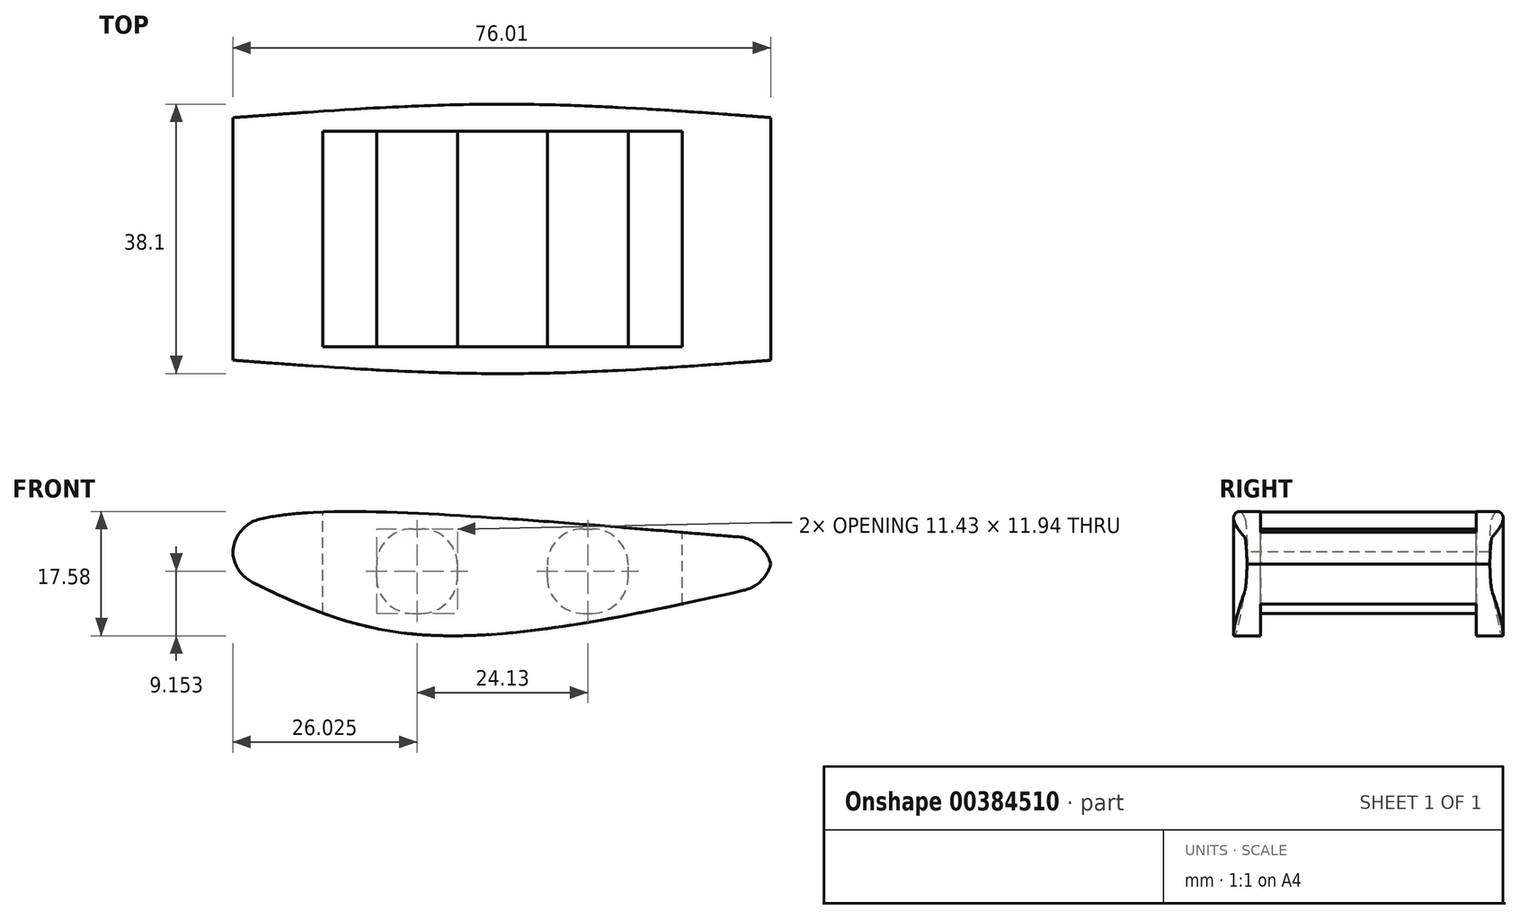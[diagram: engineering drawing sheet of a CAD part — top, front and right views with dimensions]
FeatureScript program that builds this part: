
annotation { "Feature Type Name" : "Feature", "Feature Type Description" : "" }
export const myFeature = defineFeature(function(context is Context, id is Id, definition is map)
    precondition{}
    {
        {
            var Q0;
            Q0=qCreatedBy(makeId("Top.planeOp"),FACE);
            var sketch = newSketch(context, id + "F0", { "sketchPlane" : qUnion([Q0])});
            skLineSegment(sketch, "E0.bottom", {"start": v(0, 0) * mm, "end": v(76.2, 0) * mm});
            skLineSegment(sketch, "E0.top", {"start": v(0, -38.1) * mm, "end": v(76.2, -38.1) * mm});
            skLineSegment(sketch, "E0.left", {"start": v(0, 0) * mm, "end": v(0, -38.1) * mm});
            skLineSegment(sketch, "E0.right", {"start": v(76.2, 0) * mm, "end": v(76.2, -38.1) * mm});
            skSolve(sketch);
        }
        {
            var Q0;
            Q0 = qSketchRegion(id + "F0", true);
            extrude(context, id + "F1", {"entities" : qUnion([Q0]), "depth" : 22.86 * mm});
        }
        {
            var Q0;
            Q0=makeQuery(id+"F1.opExtrude","SWEPT_FACE",FACE,{"disambiguationData":[OSD([sQuery(id+"F0.wireOp",EDGE,"E0.top")])]});
            cPlane(context, id + "F2", {"entities" : qUnion([Q0]), "cplaneType" : CPlaneType.OFFSET, "offset" : 0 * mm, "width" : 152.4 * mm, "height" : 152.4 * mm});
        }
        {
            var Q0;
            Q0=qCreatedBy(id+"F2.planeOp",FACE);
            var sketch = newSketch(context, id + "F3", { "sketchPlane" : qUnion([Q0])});
            skFitSpline(sketch, "E1", {"points": [v(0, 17.78) * mm, v(15.3, 19.73) * mm, v(76.18, 15.83) * mm, v(79.63, 15.83) * mm], "startDerivative": vector(36.87, 9.02) * mm, "endDerivative": vector(15.57, 0.79) * mm});
            skLineSegment(sketch, "E2", {"start": v(76.18, 15.83) * mm, "end": v(76.18, 9.48) * mm});
            skFitSpline(sketch, "E3", {"points": [v(76.18, 9.48) * mm, v(25.54, 2.4) * mm, v(0, 11.1) * mm], "startDerivative": vector(-95.9, -21.73) * mm, "endDerivative": vector(-55.13, 27.65) * mm});
            skLineSegment(sketch, "E4", {"start": v(0, 11.1) * mm, "end": v(0, 17.78) * mm});
            skSolve(sketch);
        }
        {
            var Q0;
            Q0=makeQuery(id+"F1.opExtrude","SWEPT_FACE",FACE,{"disambiguationData":[OSD([sQuery(id+"F0.wireOp",EDGE,"E0.top")])]});
            extrude(context, id + "F4", {"entities" : qUnion([Q0]), "operationType" : NewBodyOperationType.REMOVE, "oppositeDirection" : true, "depth" : 38.1 * mm});
        }
        {
            var Q0;
            {var subQ2=sQuery(id+"F3.wireOp",EDGE,"E2");Q0=makeQuery(id+"F3.imprint","IMPRINT",FACE,{"disambiguationData":[TD([[makeQuery(id+"F3.imprint","IMPRINT",EDGE,{"derivedFrom":subQ2}),-1.0]])]});}
            extrude(context, id + "F5", {"entities" : qUnion([Q0]), "oppositeDirection" : true, "depth" : 38.1 * mm});
        }
        {
            var Q0;
            Q0=qCreatedBy(makeId("Top.planeOp"),FACE);
            cPlane(context, id + "F6", {"entities" : qUnion([Q0]), "cplaneType" : CPlaneType.OFFSET, "offset" : 19.8 * mm, "width" : 152.4 * mm, "height" : 152.4 * mm});
        }
        {
            var Q0;
            Q0=qCreatedBy(id+"F6.planeOp",FACE);
            var sketch = newSketch(context, id + "F7", { "sketchPlane" : qUnion([Q0])});
            skLineSegment(sketch, "E5", {"start": v(0, 0) * mm, "end": v(0, -3.81) * mm});
            skLineSegment(sketch, "E6", {"start": v(0, -3.81) * mm, "end": v(76.2, -3.81) * mm});
            skLineSegment(sketch, "E7", {"start": v(0, 0) * mm, "end": v(38.1, 0) * mm});
            skLineSegment(sketch, "E8", {"start": v(76.2, -3.81) * mm, "end": v(76.2, -1.9) * mm});
            skLineSegment(sketch, "E9", {"start": v(0, -3.81) * mm, "end": v(0, -1.9) * mm});
            skFitSpline(sketch, "E10", {"points": [v(0, -1.9) * mm, v(38.1, 0) * mm, v(76.2, -1.9) * mm], "startDerivative": vector(76.2, 5.71) * mm, "endDerivative": vector(76.2, -5.71) * mm});
            skLineSegment(sketch, "E11", {"start": v(0, -3.81) * mm, "end": v(0, -34.29) * mm});
            skLineSegment(sketch, "E12", {"start": v(0, -34.29) * mm, "end": v(0, -36.2) * mm});
            skLineSegment(sketch, "E13", {"start": v(0, -34.29) * mm, "end": v(76.2, -34.29) * mm});
            skLineSegment(sketch, "E14", {"start": v(76.2, -34.29) * mm, "end": v(76.2, -36.2) * mm});
            skLineSegment(sketch, "E15", {"start": v(0, -34.29) * mm, "end": v(0, -38.1) * mm});
            skLineSegment(sketch, "E16", {"start": v(0, -38.1) * mm, "end": v(38.1, -38.1) * mm});
            skFitSpline(sketch, "E17", {"points": [v(0, -36.2) * mm, v(38.1, -38.1) * mm, v(76.2, -36.2) * mm], "startDerivative": vector(76.2, -5.71) * mm, "endDerivative": vector(76.2, 5.71) * mm});
            skLineSegment(sketch, "E18", {"start": v(38.1, 0) * mm, "end": v(76.2, 0) * mm});
            skLineSegment(sketch, "E19", {"start": v(76.2, 0) * mm, "end": v(76.2, -1.9) * mm});
            skLineSegment(sketch, "E20", {"start": v(38.1, -38.1) * mm, "end": v(76.2, -38.1) * mm});
            skLineSegment(sketch, "E21", {"start": v(76.2, -38.1) * mm, "end": v(76.2, -36.2) * mm});
            skSolve(sketch);
        }
        {
            var Q0;
            {var subQ0=sQuery(id+"F7.wireOp",EDGE,"E5");Q0=makeQuery(id+"F7.imprint","IMPRINT",FACE,{"disambiguationData":[TD([[makeQuery(id+"F7.imprint","IMPRINT",EDGE,{"derivedFrom":subQ0}),1.0]])]});}
            var Q1;
            {var subQ0=sQuery(id+"F7.wireOp",EDGE,"E16");Q1=makeQuery(id+"F7.imprint","IMPRINT",FACE,{"disambiguationData":[TD([[makeQuery(id+"F7.imprint","IMPRINT",EDGE,{"derivedFrom":subQ0}),1.0]])]});}
            var Q2;
            {var subQ2=sQuery(id+"F7.wireOp",EDGE,"E20");Q2=makeQuery(id+"F7.imprint","IMPRINT",FACE,{"disambiguationData":[TD([[makeQuery(id+"F7.imprint","IMPRINT",EDGE,{"derivedFrom":subQ2}),1.0]])]});}
            var Q3;
            {var subQ0=sQuery(id+"F7.wireOp",EDGE,"E18");Q3=makeQuery(id+"F7.imprint","IMPRINT",FACE,{"disambiguationData":[TD([[makeQuery(id+"F7.imprint","IMPRINT",EDGE,{"derivedFrom":subQ0}),-1.0]])]});}
            extrude(context, id + "F8", {"entities" : qUnion([Q0, Q1, Q2, Q3]), "operationType" : NewBodyOperationType.REMOVE, "oppositeDirection" : true, "depth" : 25.4 * mm});
        }
        {
            var Q0;
            Q0=qCreatedBy(id+"F6.planeOp",FACE);
            var sketch = newSketch(context, id + "F9", { "sketchPlane" : qUnion([Q0])});
            skLineSegment(sketch, "E22", {"start": v(0, 0) * mm, "end": v(0, -19.05) * mm});
            skLineSegment(sketch, "E23", {"start": v(0, -19.05) * mm, "end": v(12.7, -19.05) * mm});
            skLineSegment(sketch, "E24", {"start": v(12.7, -19.05) * mm, "end": v(12.7, -3.8) * mm});
            skLineSegment(sketch, "E25", {"start": v(12.7, -19.05) * mm, "end": v(12.7, -34.29) * mm});
            skLineSegment(sketch, "E26", {"start": v(63.5, -19.05) * mm, "end": v(63.5, -3.8) * mm});
            skLineSegment(sketch, "E27", {"start": v(63.5, -19.05) * mm, "end": v(63.5, -34.29) * mm});
            skLineSegment(sketch, "E28.trimOffspring", {"start": v(63.5, -19.05) * mm, "end": v(76.2, -19.05) * mm});
            skLineSegment(sketch, "E29", {"start": v(63.5, -19.05) * mm, "end": v(55.88, -19.05) * mm});
            skLineSegment(sketch, "E30", {"start": v(55.88, -19.05) * mm, "end": v(55.88, -3.8) * mm});
            skLineSegment(sketch, "E31", {"start": v(55.88, -19.05) * mm, "end": v(55.88, -34.3) * mm});
            skLineSegment(sketch, "E32", {"start": v(55.88, -34.3) * mm, "end": v(63.5, -34.3) * mm});
            skLineSegment(sketch, "E33", {"start": v(55.88, -3.8) * mm, "end": v(63.5, -3.8) * mm});
            skLineSegment(sketch, "E34", {"start": v(12.7, -19.05) * mm, "end": v(20.32, -19.05) * mm});
            skLineSegment(sketch, "E35", {"start": v(20.32, -19.05) * mm, "end": v(20.32, -3.8) * mm});
            skLineSegment(sketch, "E36", {"start": v(20.32, -19.05) * mm, "end": v(20.32, -34.29) * mm});
            skLineSegment(sketch, "E37", {"start": v(12.7, -34.29) * mm, "end": v(20.32, -34.29) * mm});
            skLineSegment(sketch, "E38", {"start": v(12.7, -3.8) * mm, "end": v(20.32, -3.8) * mm});
            skSolve(sketch);
        }
        {
            var Q0;
            Q0 = qSketchRegion(id + "F9", true);
            extrude(context, id + "F10", {"entities" : qUnion([Q0]), "operationType" : NewBodyOperationType.REMOVE, "oppositeDirection" : true, "depth" : 25.4 * mm});
        }
        {
            var Q0;
            Q0=qCreatedBy(id+"F6.planeOp",FACE);
            var sketch = newSketch(context, id + "F11", { "sketchPlane" : qUnion([Q0])});
            skLineSegment(sketch, "E39", {"start": v(0, 0) * mm, "end": v(0, -19.05) * mm});
            skLineSegment(sketch, "E40", {"start": v(31.75, -19.05) * mm, "end": v(31.75, -34.3) * mm});
            skLineSegment(sketch, "E41", {"start": v(31.75, -19.05) * mm, "end": v(31.75, -3.8) * mm});
            skLineSegment(sketch, "E42", {"start": v(44.45, -19.05) * mm, "end": v(44.45, -3.8) * mm});
            skLineSegment(sketch, "E43", {"start": v(44.45, -19.05) * mm, "end": v(44.45, -34.3) * mm});
            skLineSegment(sketch, "E44", {"start": v(31.75, -34.3) * mm, "end": v(44.45, -34.3) * mm});
            skLineSegment(sketch, "E45", {"start": v(31.75, -3.8) * mm, "end": v(44.45, -3.8) * mm});
            skSolve(sketch);
        }
        {
            var Q0;
            Q0 = qSketchRegion(id + "F11", true);
            extrude(context, id + "F12", {"entities" : qUnion([Q0]), "operationType" : NewBodyOperationType.REMOVE, "oppositeDirection" : true, "depth" : 25.4 * mm});
        }
        {
            var Q0;
            Q0=qCreatedBy(id+"F6.planeOp",FACE);
            var sketch = newSketch(context, id + "F13", { "sketchPlane" : qUnion([Q0])});
            skLineSegment(sketch, "E46", {"start": v(0, 0) * mm, "end": v(0, -19.05) * mm});
            skLineSegment(sketch, "E47", {"start": v(0, -19.05) * mm, "end": v(12.7, -19.05) * mm});
            skLineSegment(sketch, "E48", {"start": v(12.7, -19.05) * mm, "end": v(12.7, -34.3) * mm});
            skLineSegment(sketch, "E49.bottom", {"start": v(12.7, -34.3) * mm, "end": v(63.5, -34.3) * mm});
            skLineSegment(sketch, "E49.top", {"start": v(12.7, -3.8) * mm, "end": v(63.5, -3.8) * mm});
            skLineSegment(sketch, "E49.left", {"start": v(12.7, -34.3) * mm, "end": v(12.7, -3.8) * mm});
            skLineSegment(sketch, "E49.right", {"start": v(63.5, -34.29) * mm, "end": v(63.5, -3.8) * mm});
            skSolve(sketch);
        }
        {
            var Q0;
            Q0 = qSketchRegion(id + "F13", true);
            extrude(context, id + "F14", {"entities" : qUnion([Q0]), "operationType" : NewBodyOperationType.REMOVE, "depth" : -2.54 * mm});
        }
        {
            var Q0;
            Q0=makeQuery(id+"F14.boolean.opBoolean","INTERSECT",EDGE,{"derivedFrom":[makeQuery(id+"F10.boolean.opBoolean","COPY",FACE,{"derivedFrom":makeQuery(id+"F10.opExtrude","SWEPT_FACE",FACE,{"disambiguationData":[OSD([sQuery(id+"F9.wireOp",EDGE,"E30"),sQuery(id+"F9.wireOp",EDGE,"E31")])]})}),makeQuery(id+"F14.opExtrude","CAP_FACE",FACE,{"disambiguationData":[OSD([sQuery(id+"F13.wireOp",EDGE,"E49.bottom"),sQuery(id+"F13.wireOp",EDGE,"E49.top"),sQuery(id+"F13.wireOp",EDGE,"E49.left"),sQuery(id+"F13.wireOp",EDGE,"E49.right")])],"isStart":false})]});
            var Q1;
            Q1=makeQuery(id+"F14.boolean.opBoolean","INTERSECT",EDGE,{"derivedFrom":[makeQuery(id+"F12.boolean.opBoolean","COPY",FACE,{"derivedFrom":makeQuery(id+"F12.opExtrude","SWEPT_FACE",FACE,{"disambiguationData":[OSD([sQuery(id+"F11.wireOp",EDGE,"E42"),sQuery(id+"F11.wireOp",EDGE,"E43")])]})}),makeQuery(id+"F14.opExtrude","CAP_FACE",FACE,{"disambiguationData":[OSD([sQuery(id+"F13.wireOp",EDGE,"E49.bottom"),sQuery(id+"F13.wireOp",EDGE,"E49.top"),sQuery(id+"F13.wireOp",EDGE,"E49.left"),sQuery(id+"F13.wireOp",EDGE,"E49.right")])],"isStart":false})]});
            var Q2;
            Q2=makeQuery(id+"F14.boolean.opBoolean","INTERSECT",EDGE,{"derivedFrom":[makeQuery(id+"F12.boolean.opBoolean","COPY",FACE,{"derivedFrom":makeQuery(id+"F12.opExtrude","SWEPT_FACE",FACE,{"disambiguationData":[OSD([sQuery(id+"F11.wireOp",EDGE,"E40"),sQuery(id+"F11.wireOp",EDGE,"E41")])]})}),makeQuery(id+"F14.opExtrude","CAP_FACE",FACE,{"disambiguationData":[OSD([sQuery(id+"F13.wireOp",EDGE,"E49.bottom"),sQuery(id+"F13.wireOp",EDGE,"E49.top"),sQuery(id+"F13.wireOp",EDGE,"E49.left"),sQuery(id+"F13.wireOp",EDGE,"E49.right")])],"isStart":false})]});
            var Q3;
            Q3=makeQuery(id+"F14.boolean.opBoolean","INTERSECT",EDGE,{"derivedFrom":[makeQuery(id+"F10.boolean.opBoolean","COPY",FACE,{"derivedFrom":makeQuery(id+"F10.opExtrude","SWEPT_FACE",FACE,{"disambiguationData":[OSD([sQuery(id+"F9.wireOp",EDGE,"E35"),sQuery(id+"F9.wireOp",EDGE,"E36")])]})}),makeQuery(id+"F14.opExtrude","CAP_FACE",FACE,{"disambiguationData":[OSD([sQuery(id+"F13.wireOp",EDGE,"E49.bottom"),sQuery(id+"F13.wireOp",EDGE,"E49.top"),sQuery(id+"F13.wireOp",EDGE,"E49.left"),sQuery(id+"F13.wireOp",EDGE,"E49.right")])],"isStart":false})]});
            fillet(context, id + "F15", {"entities" : qUnion([Q0, Q1, Q2, Q3]), "radius" : 5.08 * mm, "tangentPropagation" : true, "allowEdgeOverflow" : false});
        }
        {
            var Q0;
            Q0=qCreatedBy(makeId("Top.planeOp"),FACE);
            var sketch = newSketch(context, id + "F16", { "sketchPlane" : qUnion([Q0])});
            skLineSegment(sketch, "E50", {"start": v(0, 0) * mm, "end": v(0, -19.05) * mm});
            skLineSegment(sketch, "E51", {"start": v(0, -19.05) * mm, "end": v(12.7, -19.05) * mm});
            skLineSegment(sketch, "E52", {"start": v(12.7, -19.05) * mm, "end": v(12.7, -3.81) * mm});
            skLineSegment(sketch, "E53.bottom", {"start": v(12.7, -3.81) * mm, "end": v(63.5, -3.81) * mm});
            skLineSegment(sketch, "E53.top", {"start": v(12.7, -34.29) * mm, "end": v(63.5, -34.29) * mm});
            skLineSegment(sketch, "E53.left", {"start": v(12.7, -3.81) * mm, "end": v(12.7, -34.29) * mm});
            skLineSegment(sketch, "E53.right", {"start": v(63.5, -3.8) * mm, "end": v(63.5, -34.3) * mm});
            skSolve(sketch);
        }
        {
            var Q0;
            Q0 = qSketchRegion(id + "F16", true);
            extrude(context, id + "F17", {"entities" : qUnion([Q0]), "operationType" : NewBodyOperationType.REMOVE, "depth" : 5.33 * mm});
        }
        {
            var Q0;
            Q0=makeQuery(id+"F17.boolean.opBoolean","INTERSECT",EDGE,{"derivedFrom":[makeQuery(id+"F10.boolean.opBoolean","COPY",FACE,{"derivedFrom":makeQuery(id+"F10.opExtrude","SWEPT_FACE",FACE,{"disambiguationData":[OSD([sQuery(id+"F9.wireOp",EDGE,"E30"),sQuery(id+"F9.wireOp",EDGE,"E31")])]})}),makeQuery(id+"F17.opExtrude","CAP_FACE",FACE,{"disambiguationData":[OSD([sQuery(id+"F16.wireOp",EDGE,"E53.bottom"),sQuery(id+"F16.wireOp",EDGE,"E53.top"),sQuery(id+"F16.wireOp",EDGE,"E53.left"),sQuery(id+"F16.wireOp",EDGE,"E53.right")])],"isStart":false})]});
            var Q1;
            Q1=makeQuery(id+"F17.boolean.opBoolean","INTERSECT",EDGE,{"derivedFrom":[makeQuery(id+"F12.boolean.opBoolean","COPY",FACE,{"derivedFrom":makeQuery(id+"F12.opExtrude","SWEPT_FACE",FACE,{"disambiguationData":[OSD([sQuery(id+"F11.wireOp",EDGE,"E42"),sQuery(id+"F11.wireOp",EDGE,"E43")])]})}),makeQuery(id+"F17.opExtrude","CAP_FACE",FACE,{"disambiguationData":[OSD([sQuery(id+"F16.wireOp",EDGE,"E53.bottom"),sQuery(id+"F16.wireOp",EDGE,"E53.top"),sQuery(id+"F16.wireOp",EDGE,"E53.left"),sQuery(id+"F16.wireOp",EDGE,"E53.right")])],"isStart":false})]});
            var Q2;
            Q2=makeQuery(id+"F17.boolean.opBoolean","INTERSECT",EDGE,{"derivedFrom":[makeQuery(id+"F10.boolean.opBoolean","COPY",FACE,{"derivedFrom":makeQuery(id+"F10.opExtrude","SWEPT_FACE",FACE,{"disambiguationData":[OSD([sQuery(id+"F9.wireOp",EDGE,"E35"),sQuery(id+"F9.wireOp",EDGE,"E36")])]})}),makeQuery(id+"F17.opExtrude","CAP_FACE",FACE,{"disambiguationData":[OSD([sQuery(id+"F16.wireOp",EDGE,"E53.bottom"),sQuery(id+"F16.wireOp",EDGE,"E53.top"),sQuery(id+"F16.wireOp",EDGE,"E53.left"),sQuery(id+"F16.wireOp",EDGE,"E53.right")])],"isStart":false})]});
            var Q3;
            Q3=makeQuery(id+"F17.boolean.opBoolean","INTERSECT",EDGE,{"derivedFrom":[makeQuery(id+"F12.boolean.opBoolean","COPY",FACE,{"derivedFrom":makeQuery(id+"F12.opExtrude","SWEPT_FACE",FACE,{"disambiguationData":[OSD([sQuery(id+"F11.wireOp",EDGE,"E40"),sQuery(id+"F11.wireOp",EDGE,"E41")])]})}),makeQuery(id+"F17.opExtrude","CAP_FACE",FACE,{"disambiguationData":[OSD([sQuery(id+"F16.wireOp",EDGE,"E53.bottom"),sQuery(id+"F16.wireOp",EDGE,"E53.top"),sQuery(id+"F16.wireOp",EDGE,"E53.left"),sQuery(id+"F16.wireOp",EDGE,"E53.right")])],"isStart":false})]});
            fillet(context, id + "F18", {"entities" : qUnion([Q0, Q1, Q2, Q3]), "radius" : 5.08 * mm, "tangentPropagation" : true, "allowEdgeOverflow" : false});
        }
        {
            var Q0;
            Q0=makeQuery(id+"F5.opExtrude","SWEPT_EDGE",EDGE,{"disambiguationData":[OSD([sQuery(id+"F3.wireOp",EDGE,"E1"),sQuery(id+"F3.wireOp",EDGE,"E2")])]});
            var Q1;
            Q1=makeQuery(id+"F5.opExtrude","SWEPT_EDGE",EDGE,{"disambiguationData":[OSD([sQuery(id+"F3.wireOp",EDGE,"E2"),sQuery(id+"F3.wireOp",EDGE,"E3")])]});
            var Q2;
            Q2=makeQuery(id+"F5.opExtrude","SWEPT_EDGE",EDGE,{"disambiguationData":[OSD([sQuery(id+"F3.wireOp",EDGE,"E1"),sQuery(id+"F3.wireOp",EDGE,"E4")])]});
            var Q3;
            Q3=makeQuery(id+"F5.opExtrude","SWEPT_EDGE",EDGE,{"disambiguationData":[OSD([sQuery(id+"F3.wireOp",EDGE,"E3"),sQuery(id+"F3.wireOp",EDGE,"E4")])]});
            fillet(context, id + "F19", {"entities" : qUnion([Q0, Q1, Q2, Q3]), "radius" : 5.08 * mm, "tangentPropagation" : true, "allowEdgeOverflow" : false});
        }
    });
